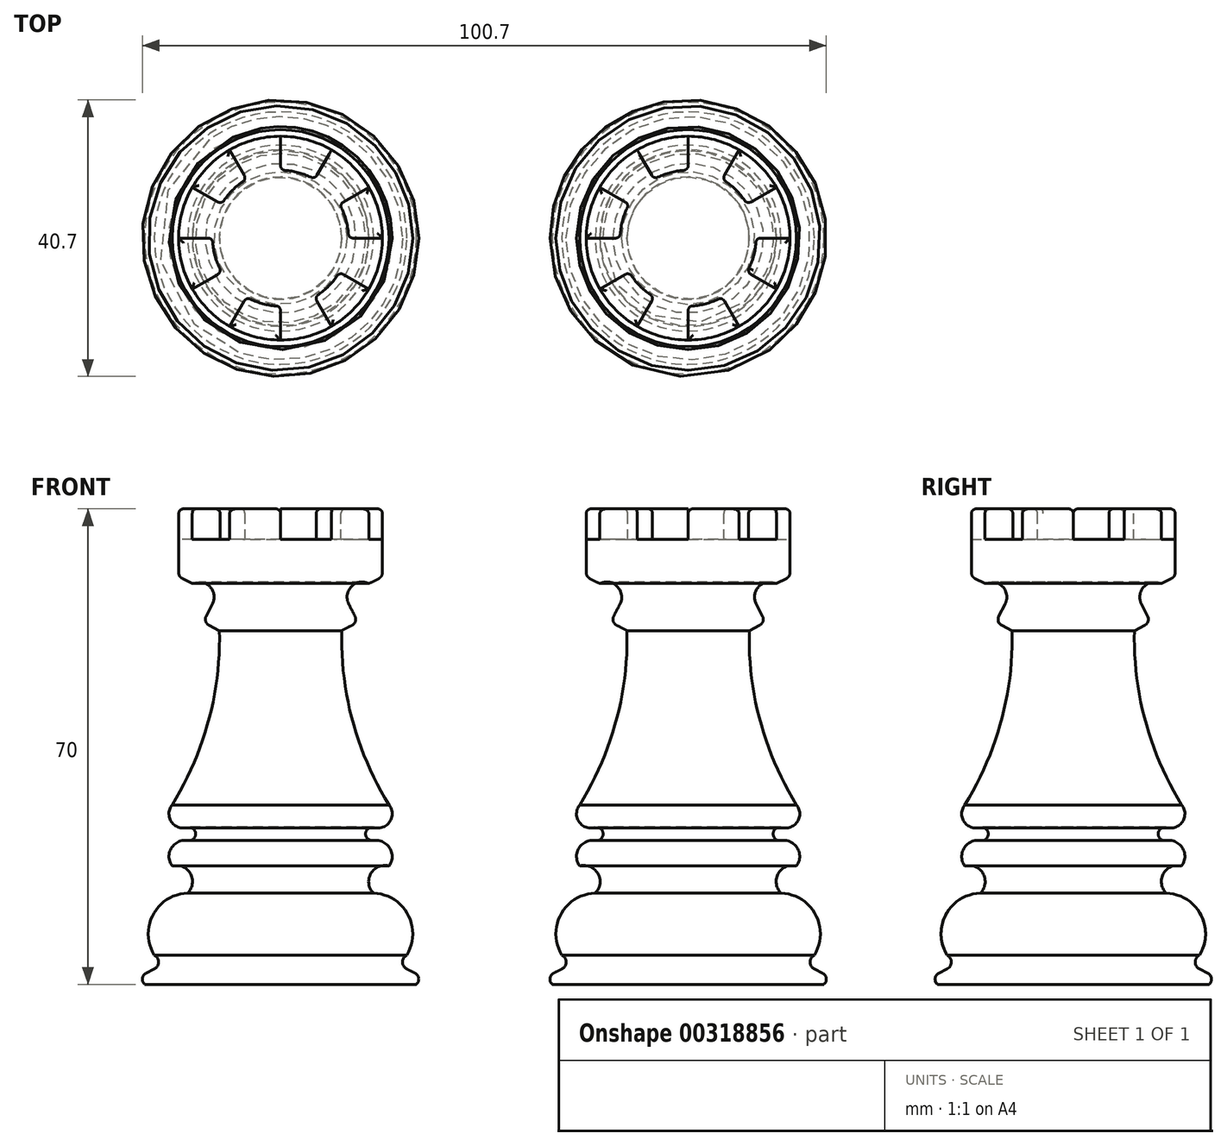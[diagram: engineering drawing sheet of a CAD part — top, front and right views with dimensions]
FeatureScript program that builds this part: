
annotation { "Feature Type Name" : "Feature", "Feature Type Description" : "" }
export const myFeature = defineFeature(function(context is Context, id is Id, definition is map)
    precondition{}
    {
        {
            var Q0;
            Q0=qCreatedBy(makeId("Front.planeOp"),FACE);
            var sketch = newSketch(context, id + "F0", { "sketchPlane" : qUnion([Q0])});
            skLineSegment(sketch, "E0", {"start": v(0, 35) * mm, "end": v(0, -35) * mm});
            skLineSegment(sketch, "E1", {"start": v(0, -35) * mm, "end": v(-20, -35) * mm});
            skLineSegment(sketch, "E2", {"start": v(0, 35) * mm, "end": v(-15, 35) * mm});
            skLineSegment(sketch, "E3", {"start": v(-15, 35) * mm, "end": v(-15, 25) * mm});
            skLineSegment(sketch, "E4", {"start": v(-20, -35) * mm, "end": v(-21.1, -34) * mm});
            skLineSegment(sketch, "E5", {"start": v(-21.1, -34) * mm, "end": v(-18.59, -32.74) * mm});
            skArc(sketch, "E6", {"start": v(-18.59, -32.74) * mm, "mid": v(-17.95, -31.72) * mm, "end": v(-18.59, -30.69) * mm});
            skArc(sketch, "E7", {"start": v(-13.69, -21.57) * mm, "mid": v(-18.76, -24.72) * mm, "end": v(-18.59, -30.69) * mm});
            skArc(sketch, "E8", {"start": v(-13.69, -21.57) * mm, "mid": v(-13.28, -18.7) * mm, "end": v(-15.97, -17.59) * mm});
            skArc(sketch, "E9", {"start": v(-13.69, -13.82) * mm, "mid": v(-16.08, -14.95) * mm, "end": v(-15.97, -17.59) * mm});
            skArc(sketch, "E10", {"start": v(-13.69, -13.82) * mm, "mid": v(-12.51, -12.86) * mm, "end": v(-13.69, -11.89) * mm});
            skArc(sketch, "E11", {"start": v(-15.97, -8.58) * mm, "mid": v(-16.06, -11.09) * mm, "end": v(-13.69, -11.89) * mm});
            skPoint(sketch, "E12.center.orphan", {"position": v(-14.66, 21) * mm});
            skPoint(sketch, "E12.end.orphan", {"position": v(-13, 24) * mm});
            skPoint(sketch, "E13.start.orphan", {"position": v(-9, 20.16) * mm});
            skPoint(sketch, "E14.end.orphan", {"position": v(-9, 17.08) * mm});
            skArc(sketch, "E15", {"start": v(-15.97, -8.58) * mm, "mid": v(-10.62, 3.74) * mm, "end": v(-9, 17.08) * mm});
            skLineSegment(sketch, "E16", {"start": v(-9, 17.08) * mm, "end": v(-11.4, 18.3) * mm});
            skLineSegment(sketch, "E17", {"start": v(-11.4, 18.3) * mm, "end": v(-10.03, 21) * mm});
            skArc(sketch, "E18", {"start": v(-10.03, 21) * mm, "mid": v(-10.43, 23.58) * mm, "end": v(-13, 24) * mm});
            skLineSegment(sketch, "E19", {"start": v(-15, 25) * mm, "end": v(-13, 24) * mm});
            skLineSegment(sketch, "E20", {"start": v(0, 44.63) * mm, "end": v(0, -39) * mm, "construction": true});
            skSolve(sketch);
        }
        {
            var Q0;
            Q0=makeQuery(id+"F0.imprint","IMPRINT",FACE,{"disambiguationData":[TD([[makeQuery(id+"F0.imprint","IMPRINT",EDGE,{"derivedFrom":sQuery(id+"F0.wireOp",EDGE,"E0")}),-1.0]])]});
            var Q1;
            Q1=sQuery(id+"F0.wireOp",EDGE,"E20");
            revolve(context, id + "F1", {"entities" : qUnion([Q0]), "axis" : qUnion([Q1]), "revolveType" : RevolveType.FULL});
        }
        {
            var Q0;
            Q0=makeQuery(id+"F1.opRevolve","SWEPT_EDGE",EDGE,{"disambiguationData":[OSD([sQuery(id+"F0.wireOp",EDGE,"E4"),sQuery(id+"F0.wireOp",EDGE,"E5")])]});
            var Q1;
            Q1=makeQuery(id+"F1.opRevolve","SWEPT_EDGE",EDGE,{"disambiguationData":[OSD([sQuery(id+"F0.wireOp",EDGE,"E16"),sQuery(id+"F0.wireOp",EDGE,"E17")])]});
            var Q2;
            Q2=makeQuery(id+"F1.opRevolve","SWEPT_EDGE",EDGE,{"disambiguationData":[OSD([sQuery(id+"F0.wireOp",EDGE,"E3"),sQuery(id+"F0.wireOp",EDGE,"E19")])]});
            fillet(context, id + "F2", {"entities" : qUnion([Q0, Q1, Q2]), "radius" : 1 * mm, "tangentPropagation" : true, "allowEdgeOverflow" : false});
        }
        {
            var Q0;
            Q0=qCreatedBy(makeId("Right.planeOp"),FACE);
            cPlane(context, id + "F3", {"entities" : qUnion([Q0]), "cplaneType" : CPlaneType.OFFSET, "offset" : 30 * mm, "width" : 150 * mm, "height" : 150 * mm});
        }
        {
            var Q0;
            Q0=makeQuery(id+"F1.opRevolve","SWEPT_FACE",FACE,{"disambiguationData":[OSD([sQuery(id+"F0.wireOp",EDGE,"E2")])]});
            var sketch = newSketch(context, id + "F4", { "sketchPlane" : qUnion([Q0])});
            skArc(sketch, "E21.0", {"start": v(5, 8.66) * mm, "mid": v(2.59, 9.66) * mm, "end": v(0, 10) * mm});
            skArc(sketch, "E22.cCircle", {"start": v(5, 8.66) * mm, "mid": v(2.59, 9.66) * mm, "end": v(0, 10) * mm, "construction": true});
            skLineSegment(sketch, "E22.0", {"start": v(0, 10) * mm, "end": v(5, 8.66) * mm, "construction": true});
            skLineSegment(sketch, "E22.2", {"start": v(8.66, 5) * mm, "end": v(10, 0) * mm, "construction": true});
            skLineSegment(sketch, "E22.4", {"start": v(8.66, -5) * mm, "end": v(5, -8.66) * mm, "construction": true});
            skLineSegment(sketch, "E22.6", {"start": v(0, -10) * mm, "end": v(-5, -8.66) * mm, "construction": true});
            skLineSegment(sketch, "E22.8", {"start": v(-8.66, -5) * mm, "end": v(-10, 0) * mm, "construction": true});
            skLineSegment(sketch, "E22.10", {"start": v(-8.66, 5) * mm, "end": v(-5, 8.66) * mm, "construction": true});
            skCircle(sketch, "E23.cCircle", {"center": v(0, 0) * mm, "radius": 15 * mm, "construction": true});
            skLineSegment(sketch, "E23.0", {"start": v(0, 15) * mm, "end": v(7.5, 13) * mm, "construction": true});
            skLineSegment(sketch, "E23.1", {"start": v(7.5, 13) * mm, "end": v(13, 7.5) * mm, "construction": true});
            skLineSegment(sketch, "E23.2", {"start": v(13, 7.5) * mm, "end": v(15, 0) * mm, "construction": true});
            skLineSegment(sketch, "E23.3", {"start": v(15, 0) * mm, "end": v(13, -7.5) * mm, "construction": true});
            skLineSegment(sketch, "E23.4", {"start": v(13, -7.5) * mm, "end": v(7.5, -13) * mm, "construction": true});
            skLineSegment(sketch, "E23.5", {"start": v(7.5, -13) * mm, "end": v(0, -15) * mm, "construction": true});
            skLineSegment(sketch, "E23.6", {"start": v(0, -15) * mm, "end": v(-7.5, -13) * mm, "construction": true});
            skLineSegment(sketch, "E23.7", {"start": v(-7.5, -13) * mm, "end": v(-13, -7.5) * mm, "construction": true});
            skLineSegment(sketch, "E23.8", {"start": v(-13, -7.5) * mm, "end": v(-15, 0) * mm, "construction": true});
            skLineSegment(sketch, "E23.9", {"start": v(-15, 0) * mm, "end": v(-13, 7.5) * mm, "construction": true});
            skLineSegment(sketch, "E23.10", {"start": v(-13, 7.5) * mm, "end": v(-7.5, 13) * mm, "construction": true});
            skLineSegment(sketch, "E23.11", {"start": v(-7.5, 13) * mm, "end": v(0, 15) * mm, "construction": true});
            skLineSegment(sketch, "E24", {"start": v(0, 10) * mm, "end": v(0, 15) * mm});
            skLineSegment(sketch, "E25", {"start": v(5, 8.66) * mm, "end": v(7.5, 13) * mm});
            skLineSegment(sketch, "E26", {"start": v(8.66, 5) * mm, "end": v(13, 7.5) * mm});
            skLineSegment(sketch, "E27", {"start": v(10, 0) * mm, "end": v(15, 0) * mm});
            skLineSegment(sketch, "E28", {"start": v(8.66, -5) * mm, "end": v(13, -7.5) * mm});
            skLineSegment(sketch, "E29", {"start": v(5, -8.66) * mm, "end": v(7.5, -13) * mm});
            skLineSegment(sketch, "E30", {"start": v(0, -10) * mm, "end": v(0, -15) * mm});
            skLineSegment(sketch, "E31", {"start": v(-5, -8.66) * mm, "end": v(-7.5, -13) * mm});
            skLineSegment(sketch, "E32", {"start": v(-8.66, -5) * mm, "end": v(-13, -7.5) * mm});
            skLineSegment(sketch, "E33", {"start": v(-10, 0) * mm, "end": v(-15, 0) * mm});
            skLineSegment(sketch, "E34", {"start": v(-8.66, 5) * mm, "end": v(-13, 7.5) * mm});
            skLineSegment(sketch, "E35", {"start": v(-5, 8.66) * mm, "end": v(-7.5, 13) * mm});
            skArc(sketch, "E36.trimOffspring", {"start": v(10, 0) * mm, "mid": v(9.66, 2.59) * mm, "end": v(8.66, 5) * mm, "construction": true});
            skArc(sketch, "E37.trimOffspring", {"start": v(10, 0) * mm, "mid": v(9.66, 2.59) * mm, "end": v(8.66, 5) * mm});
            skArc(sketch, "E38.trimOffspring", {"start": v(5, -8.66) * mm, "mid": v(7.07, -7.07) * mm, "end": v(8.66, -5) * mm, "construction": true});
            skArc(sketch, "E39.trimOffspring", {"start": v(5, -8.66) * mm, "mid": v(7.07, -7.07) * mm, "end": v(8.66, -5) * mm});
            skArc(sketch, "E40.trimOffspring", {"start": v(-5, -8.66) * mm, "mid": v(-2.59, -9.66) * mm, "end": v(0, -10) * mm, "construction": true});
            skArc(sketch, "E41.trimOffspring", {"start": v(-5, -8.66) * mm, "mid": v(-2.59, -9.66) * mm, "end": v(0, -10) * mm});
            skArc(sketch, "E42.trimOffspring", {"start": v(-10, 0) * mm, "mid": v(-9.66, -2.59) * mm, "end": v(-8.66, -5) * mm, "construction": true});
            skArc(sketch, "E43.trimOffspring", {"start": v(-10, 0) * mm, "mid": v(-9.66, -2.59) * mm, "end": v(-8.66, -5) * mm});
            skArc(sketch, "E44.trimOffspring", {"start": v(-5, 8.66) * mm, "mid": v(-7.07, 7.07) * mm, "end": v(-8.66, 5) * mm, "construction": true});
            skArc(sketch, "E45.trimOffspring", {"start": v(-5, 8.66) * mm, "mid": v(-7.07, 7.07) * mm, "end": v(-8.66, 5) * mm});
            skSolve(sketch);
        }
        {
            var Q0;
            Q0=makeQuery(id+"F4.imprint","IMPRINT",FACE,{"disambiguationData":[TD([[makeQuery(id+"F4.imprint","IMPRINT",EDGE,{"derivedFrom":sQuery(id+"F4.wireOp",EDGE,"E21.0")}),1.0]])]});
            extrude(context, id + "F5", {"entities" : qUnion([Q0]), "operationType" : NewBodyOperationType.REMOVE, "oppositeDirection" : true, "depth" : 4.5 * mm});
        }
        {
            var Q0;
            {var subQ0=sQuery(id+"F0.wireOp",EDGE,"E3");var subQ1=sQuery(id+"F0.wireOp",EDGE,"E2");var subQ2=makeQuery(id+"F1.opRevolve","SWEPT_EDGE",EDGE,{"disambiguationData":[OSD([subQ1,subQ0])]});Q0=makeQuery(id+"F5.boolean.opBoolean","COPY",EDGE,{"derivedFrom":makeQuery(id+"F5.opExtrude","CAP_EDGE",EDGE,{"disambiguationData":[OSD([subQ1,subQ0]),TDD([makeQuery(id+"F4.imprint","IMPRINT",EDGE,{"disambiguationData":[TD([[makeQuery(id+"F4.imprint","INTERSECT",VERTEX,{"derivedFrom":[subQ2,sQuery(id+"F4.wireOp",EDGE,"E27")]}),1.0]])],"derivedFrom":subQ2})])],"isStart":false})});}
            var Q1;
            Q1=makeQuery(id+"F5.boolean.opBoolean","COPY",EDGE,{"derivedFrom":makeQuery(id+"F5.opExtrude","SWEPT_EDGE",EDGE,{"disambiguationData":[OSD([sQuery(id+"F0.wireOp",EDGE,"E2"),sQuery(id+"F0.wireOp",EDGE,"E3"),sQuery(id+"F4.wireOp",EDGE,"E28")])]})});
            var Q2;
            {var subQ0=sQuery(id+"F0.wireOp",EDGE,"E3");var subQ1=sQuery(id+"F0.wireOp",EDGE,"E2");var subQ2=makeQuery(id+"F1.opRevolve","SWEPT_EDGE",EDGE,{"disambiguationData":[OSD([subQ1,subQ0])]});Q2=makeQuery(id+"F5.boolean.opBoolean","COPY",EDGE,{"derivedFrom":makeQuery(id+"F5.opExtrude","CAP_EDGE",EDGE,{"disambiguationData":[OSD([subQ1,subQ0]),TDD([makeQuery(id+"F4.imprint","IMPRINT",EDGE,{"disambiguationData":[TD([[makeQuery(id+"F4.imprint","INTERSECT",VERTEX,{"derivedFrom":[subQ2,sQuery(id+"F4.wireOp",EDGE,"E29")]}),1.0]])],"derivedFrom":subQ2})])],"isStart":false})});}
            var Q3;
            Q3=makeQuery(id+"F5.boolean.opBoolean","COPY",EDGE,{"derivedFrom":makeQuery(id+"F5.opExtrude","SWEPT_EDGE",EDGE,{"disambiguationData":[OSD([sQuery(id+"F0.wireOp",EDGE,"E2"),sQuery(id+"F0.wireOp",EDGE,"E3"),sQuery(id+"F4.wireOp",EDGE,"E29")])]})});
            var Q4;
            {var subQ0=sQuery(id+"F0.wireOp",EDGE,"E2");var subQ1=sQuery(id+"F0.wireOp",EDGE,"E3");Q4=makeQuery(id+"F5.boolean.opBoolean","SPLIT",EDGE,{"disambiguationData":[TD([makeQuery(id+"F5.opExtrude","SWEPT_FACE",FACE,{"disambiguationData":[OSD([sQuery(id+"F4.wireOp",EDGE,"E28")])]})])],"derivedFrom":makeQuery(id+"F1.opRevolve","SWEPT_EDGE",EDGE,{"disambiguationData":[OSD([subQ0,subQ1])]})});}
            var Q5;
            Q5=makeQuery(id+"F5.boolean.opBoolean","COPY",EDGE,{"derivedFrom":makeQuery(id+"F5.opExtrude","SWEPT_EDGE",EDGE,{"disambiguationData":[OSD([sQuery(id+"F0.wireOp",EDGE,"E2"),sQuery(id+"F0.wireOp",EDGE,"E3"),sQuery(id+"F4.wireOp",EDGE,"E30")])]})});
            var Q6;
            {var subQ0=sQuery(id+"F0.wireOp",EDGE,"E2");var subQ1=sQuery(id+"F0.wireOp",EDGE,"E3");Q6=makeQuery(id+"F5.boolean.opBoolean","SPLIT",EDGE,{"disambiguationData":[TD([makeQuery(id+"F5.opExtrude","SWEPT_FACE",FACE,{"disambiguationData":[OSD([sQuery(id+"F4.wireOp",EDGE,"E30")])]})])],"derivedFrom":makeQuery(id+"F1.opRevolve","SWEPT_EDGE",EDGE,{"disambiguationData":[OSD([subQ0,subQ1])]})});}
            var Q7;
            Q7=makeQuery(id+"F5.boolean.opBoolean","COPY",EDGE,{"derivedFrom":makeQuery(id+"F5.opExtrude","SWEPT_EDGE",EDGE,{"disambiguationData":[OSD([sQuery(id+"F0.wireOp",EDGE,"E2"),sQuery(id+"F0.wireOp",EDGE,"E3"),sQuery(id+"F4.wireOp",EDGE,"E31")])]})});
            var Q8;
            {var subQ0=sQuery(id+"F0.wireOp",EDGE,"E3");var subQ1=sQuery(id+"F0.wireOp",EDGE,"E2");var subQ2=makeQuery(id+"F1.opRevolve","SWEPT_EDGE",EDGE,{"disambiguationData":[OSD([subQ1,subQ0])]});Q8=makeQuery(id+"F5.boolean.opBoolean","COPY",EDGE,{"derivedFrom":makeQuery(id+"F5.opExtrude","CAP_EDGE",EDGE,{"disambiguationData":[OSD([subQ1,subQ0]),TDD([makeQuery(id+"F4.imprint","IMPRINT",EDGE,{"disambiguationData":[TD([[makeQuery(id+"F4.imprint","INTERSECT",VERTEX,{"derivedFrom":[subQ2,sQuery(id+"F4.wireOp",EDGE,"E31")]}),1.0]])],"derivedFrom":subQ2})])],"isStart":false})});}
            var Q9;
            Q9=makeQuery(id+"F5.boolean.opBoolean","COPY",EDGE,{"derivedFrom":makeQuery(id+"F5.opExtrude","SWEPT_EDGE",EDGE,{"disambiguationData":[OSD([sQuery(id+"F0.wireOp",EDGE,"E2"),sQuery(id+"F0.wireOp",EDGE,"E3"),sQuery(id+"F4.wireOp",EDGE,"E32")])]})});
            var Q10;
            {var subQ0=sQuery(id+"F0.wireOp",EDGE,"E2");var subQ1=sQuery(id+"F0.wireOp",EDGE,"E3");Q10=makeQuery(id+"F5.boolean.opBoolean","SPLIT",EDGE,{"disambiguationData":[TD([makeQuery(id+"F5.opExtrude","SWEPT_FACE",FACE,{"disambiguationData":[OSD([sQuery(id+"F4.wireOp",EDGE,"E32")])]})])],"derivedFrom":makeQuery(id+"F1.opRevolve","SWEPT_EDGE",EDGE,{"disambiguationData":[OSD([subQ0,subQ1])]})});}
            var Q11;
            {var subQ0=sQuery(id+"F0.wireOp",EDGE,"E3");var subQ1=sQuery(id+"F0.wireOp",EDGE,"E2");var subQ2=makeQuery(id+"F1.opRevolve","SWEPT_EDGE",EDGE,{"disambiguationData":[OSD([subQ1,subQ0])]});Q11=makeQuery(id+"F5.boolean.opBoolean","COPY",EDGE,{"derivedFrom":makeQuery(id+"F5.opExtrude","CAP_EDGE",EDGE,{"disambiguationData":[OSD([subQ1,subQ0]),TDD([makeQuery(id+"F4.imprint","IMPRINT",EDGE,{"disambiguationData":[TD([[makeQuery(id+"F4.imprint","INTERSECT",VERTEX,{"derivedFrom":[subQ2,sQuery(id+"F4.wireOp",EDGE,"E33")]}),1.0]])],"derivedFrom":subQ2})])],"isStart":false})});}
            var Q12;
            {var subQ0=sQuery(id+"F0.wireOp",EDGE,"E3");var subQ1=sQuery(id+"F0.wireOp",EDGE,"E2");var subQ2=makeQuery(id+"F1.opRevolve","SWEPT_EDGE",EDGE,{"disambiguationData":[OSD([subQ1,subQ0])]});Q12=makeQuery(id+"F5.boolean.opBoolean","COPY",EDGE,{"derivedFrom":makeQuery(id+"F5.opExtrude","CAP_EDGE",EDGE,{"disambiguationData":[OSD([subQ1,subQ0]),TDD([makeQuery(id+"F4.imprint","IMPRINT",EDGE,{"disambiguationData":[TD([[makeQuery(id+"F4.imprint","INTERSECT",VERTEX,{"derivedFrom":[subQ2,sQuery(id+"F4.wireOp",EDGE,"E24")]}),-1.0]])],"derivedFrom":subQ2})])],"isStart":false})});}
            var Q13;
            {var subQ0=sQuery(id+"F0.wireOp",EDGE,"E3");var subQ1=sQuery(id+"F0.wireOp",EDGE,"E2");var subQ2=makeQuery(id+"F1.opRevolve","SWEPT_EDGE",EDGE,{"disambiguationData":[OSD([subQ1,subQ0])]});Q13=makeQuery(id+"F5.boolean.opBoolean","COPY",EDGE,{"derivedFrom":makeQuery(id+"F5.opExtrude","CAP_EDGE",EDGE,{"disambiguationData":[OSD([subQ1,subQ0]),TDD([makeQuery(id+"F4.imprint","IMPRINT",EDGE,{"disambiguationData":[TD([[makeQuery(id+"F4.imprint","INTERSECT",VERTEX,{"derivedFrom":[subQ2,sQuery(id+"F4.wireOp",EDGE,"E25")]}),1.0]])],"derivedFrom":subQ2})])],"isStart":false})});}
            var Q14;
            {var subQ0=sQuery(id+"F0.wireOp",EDGE,"E2");var subQ1=sQuery(id+"F0.wireOp",EDGE,"E3");Q14=makeQuery(id+"F5.boolean.opBoolean","SPLIT",EDGE,{"disambiguationData":[TD([makeQuery(id+"F5.opExtrude","SWEPT_FACE",FACE,{"disambiguationData":[OSD([sQuery(id+"F4.wireOp",EDGE,"E34")])]})])],"derivedFrom":makeQuery(id+"F1.opRevolve","SWEPT_EDGE",EDGE,{"disambiguationData":[OSD([subQ0,subQ1])]})});}
            var Q15;
            {var subQ0=sQuery(id+"F0.wireOp",EDGE,"E2");var subQ1=sQuery(id+"F0.wireOp",EDGE,"E3");Q15=makeQuery(id+"F5.boolean.opBoolean","SPLIT",EDGE,{"disambiguationData":[TD([makeQuery(id+"F5.opExtrude","SWEPT_FACE",FACE,{"disambiguationData":[OSD([sQuery(id+"F4.wireOp",EDGE,"E24")])]})])],"derivedFrom":makeQuery(id+"F1.opRevolve","SWEPT_EDGE",EDGE,{"disambiguationData":[OSD([subQ0,subQ1])]})});}
            var Q16;
            {var subQ0=sQuery(id+"F0.wireOp",EDGE,"E2");var subQ1=sQuery(id+"F0.wireOp",EDGE,"E3");Q16=makeQuery(id+"F5.boolean.opBoolean","SPLIT",EDGE,{"disambiguationData":[TD([makeQuery(id+"F5.opExtrude","SWEPT_FACE",FACE,{"disambiguationData":[OSD([sQuery(id+"F4.wireOp",EDGE,"E26")])]})])],"derivedFrom":makeQuery(id+"F1.opRevolve","SWEPT_EDGE",EDGE,{"disambiguationData":[OSD([subQ0,subQ1])]})});}
            var Q17;
            Q17=makeQuery(id+"F5.boolean.opBoolean","COPY",EDGE,{"derivedFrom":makeQuery(id+"F5.opExtrude","CAP_EDGE",EDGE,{"disambiguationData":[OSD([sQuery(id+"F4.wireOp",EDGE,"E24")])],"isStart":true})});
            var Q18;
            Q18=makeQuery(id+"F5.boolean.opBoolean","COPY",EDGE,{"derivedFrom":makeQuery(id+"F5.opExtrude","CAP_EDGE",EDGE,{"disambiguationData":[OSD([sQuery(id+"F4.wireOp",EDGE,"E21.0")])],"isStart":true})});
            var Q19;
            Q19=makeQuery(id+"F5.boolean.opBoolean","COPY",EDGE,{"derivedFrom":makeQuery(id+"F5.opExtrude","CAP_EDGE",EDGE,{"disambiguationData":[OSD([sQuery(id+"F4.wireOp",EDGE,"E25")])],"isStart":true})});
            var Q20;
            Q20=makeQuery(id+"F5.boolean.opBoolean","COPY",EDGE,{"derivedFrom":makeQuery(id+"F5.opExtrude","CAP_EDGE",EDGE,{"disambiguationData":[OSD([sQuery(id+"F4.wireOp",EDGE,"E26")])],"isStart":true})});
            var Q21;
            Q21=makeQuery(id+"F5.boolean.opBoolean","COPY",EDGE,{"derivedFrom":makeQuery(id+"F5.opExtrude","CAP_EDGE",EDGE,{"disambiguationData":[OSD([sQuery(id+"F4.wireOp",EDGE,"E37.trimOffspring")])],"isStart":true})});
            var Q22;
            Q22=makeQuery(id+"F5.boolean.opBoolean","COPY",EDGE,{"derivedFrom":makeQuery(id+"F5.opExtrude","CAP_EDGE",EDGE,{"disambiguationData":[OSD([sQuery(id+"F4.wireOp",EDGE,"E27")])],"isStart":true})});
            var Q23;
            Q23=makeQuery(id+"F5.boolean.opBoolean","COPY",EDGE,{"derivedFrom":makeQuery(id+"F5.opExtrude","CAP_EDGE",EDGE,{"disambiguationData":[OSD([sQuery(id+"F4.wireOp",EDGE,"E28")])],"isStart":true})});
            var Q24;
            Q24=makeQuery(id+"F5.boolean.opBoolean","COPY",EDGE,{"derivedFrom":makeQuery(id+"F5.opExtrude","CAP_EDGE",EDGE,{"disambiguationData":[OSD([sQuery(id+"F4.wireOp",EDGE,"E39.trimOffspring")])],"isStart":true})});
            var Q25;
            Q25=makeQuery(id+"F5.boolean.opBoolean","COPY",EDGE,{"derivedFrom":makeQuery(id+"F5.opExtrude","CAP_EDGE",EDGE,{"disambiguationData":[OSD([sQuery(id+"F4.wireOp",EDGE,"E29")])],"isStart":true})});
            var Q26;
            Q26=makeQuery(id+"F5.boolean.opBoolean","COPY",EDGE,{"derivedFrom":makeQuery(id+"F5.opExtrude","CAP_EDGE",EDGE,{"disambiguationData":[OSD([sQuery(id+"F4.wireOp",EDGE,"E30")])],"isStart":true})});
            var Q27;
            Q27=makeQuery(id+"F5.boolean.opBoolean","COPY",EDGE,{"derivedFrom":makeQuery(id+"F5.opExtrude","CAP_EDGE",EDGE,{"disambiguationData":[OSD([sQuery(id+"F4.wireOp",EDGE,"E41.trimOffspring")])],"isStart":true})});
            var Q28;
            Q28=makeQuery(id+"F5.boolean.opBoolean","COPY",EDGE,{"derivedFrom":makeQuery(id+"F5.opExtrude","CAP_EDGE",EDGE,{"disambiguationData":[OSD([sQuery(id+"F4.wireOp",EDGE,"E31")])],"isStart":true})});
            var Q29;
            Q29=makeQuery(id+"F5.boolean.opBoolean","COPY",EDGE,{"derivedFrom":makeQuery(id+"F5.opExtrude","CAP_EDGE",EDGE,{"disambiguationData":[OSD([sQuery(id+"F4.wireOp",EDGE,"E32")])],"isStart":true})});
            var Q30;
            Q30=makeQuery(id+"F5.boolean.opBoolean","COPY",EDGE,{"derivedFrom":makeQuery(id+"F5.opExtrude","CAP_EDGE",EDGE,{"disambiguationData":[OSD([sQuery(id+"F4.wireOp",EDGE,"E43.trimOffspring")])],"isStart":true})});
            var Q31;
            Q31=makeQuery(id+"F5.boolean.opBoolean","COPY",EDGE,{"derivedFrom":makeQuery(id+"F5.opExtrude","CAP_EDGE",EDGE,{"disambiguationData":[OSD([sQuery(id+"F4.wireOp",EDGE,"E33")])],"isStart":true})});
            var Q32;
            Q32=makeQuery(id+"F5.boolean.opBoolean","COPY",EDGE,{"derivedFrom":makeQuery(id+"F5.opExtrude","CAP_EDGE",EDGE,{"disambiguationData":[OSD([sQuery(id+"F4.wireOp",EDGE,"E34")])],"isStart":true})});
            var Q33;
            Q33=makeQuery(id+"F5.boolean.opBoolean","COPY",EDGE,{"derivedFrom":makeQuery(id+"F5.opExtrude","CAP_EDGE",EDGE,{"disambiguationData":[OSD([sQuery(id+"F4.wireOp",EDGE,"E45.trimOffspring")])],"isStart":true})});
            var Q34;
            Q34=makeQuery(id+"F5.boolean.opBoolean","COPY",EDGE,{"derivedFrom":makeQuery(id+"F5.opExtrude","CAP_EDGE",EDGE,{"disambiguationData":[OSD([sQuery(id+"F4.wireOp",EDGE,"E35")])],"isStart":true})});
            var Q35;
            Q35=makeQuery(id+"F5.boolean.opBoolean","COPY",EDGE,{"derivedFrom":makeQuery(id+"F5.opExtrude","SWEPT_EDGE",EDGE,{"disambiguationData":[OSD([sQuery(id+"F0.wireOp",EDGE,"E2"),sQuery(id+"F0.wireOp",EDGE,"E3"),sQuery(id+"F4.wireOp",EDGE,"E33")])]})});
            var Q36;
            Q36=makeQuery(id+"F5.boolean.opBoolean","COPY",EDGE,{"derivedFrom":makeQuery(id+"F5.opExtrude","SWEPT_EDGE",EDGE,{"disambiguationData":[OSD([sQuery(id+"F0.wireOp",EDGE,"E2"),sQuery(id+"F0.wireOp",EDGE,"E3"),sQuery(id+"F4.wireOp",EDGE,"E34")])]})});
            var Q37;
            Q37=makeQuery(id+"F5.boolean.opBoolean","COPY",EDGE,{"derivedFrom":makeQuery(id+"F5.opExtrude","SWEPT_EDGE",EDGE,{"disambiguationData":[OSD([sQuery(id+"F0.wireOp",EDGE,"E2"),sQuery(id+"F0.wireOp",EDGE,"E3"),sQuery(id+"F4.wireOp",EDGE,"E35")])]})});
            var Q38;
            Q38=makeQuery(id+"F5.boolean.opBoolean","COPY",EDGE,{"derivedFrom":makeQuery(id+"F5.opExtrude","SWEPT_EDGE",EDGE,{"disambiguationData":[OSD([sQuery(id+"F0.wireOp",EDGE,"E2"),sQuery(id+"F0.wireOp",EDGE,"E3"),sQuery(id+"F4.wireOp",EDGE,"E24")])]})});
            var Q39;
            Q39=makeQuery(id+"F5.boolean.opBoolean","COPY",EDGE,{"derivedFrom":makeQuery(id+"F5.opExtrude","SWEPT_EDGE",EDGE,{"disambiguationData":[OSD([sQuery(id+"F0.wireOp",EDGE,"E2"),sQuery(id+"F0.wireOp",EDGE,"E3"),sQuery(id+"F4.wireOp",EDGE,"E25")])]})});
            var Q40;
            Q40=makeQuery(id+"F5.boolean.opBoolean","COPY",EDGE,{"derivedFrom":makeQuery(id+"F5.opExtrude","SWEPT_EDGE",EDGE,{"disambiguationData":[OSD([sQuery(id+"F0.wireOp",EDGE,"E2"),sQuery(id+"F0.wireOp",EDGE,"E3"),sQuery(id+"F4.wireOp",EDGE,"E26")])]})});
            var Q41;
            Q41=makeQuery(id+"F5.boolean.opBoolean","COPY",EDGE,{"derivedFrom":makeQuery(id+"F5.opExtrude","SWEPT_EDGE",EDGE,{"disambiguationData":[OSD([sQuery(id+"F0.wireOp",EDGE,"E2"),sQuery(id+"F0.wireOp",EDGE,"E3"),sQuery(id+"F4.wireOp",EDGE,"E27")])]})});
            var Q42;
            Q42=makeQuery(id+"F5.boolean.opBoolean","COPY",EDGE,{"derivedFrom":makeQuery(id+"F5.opExtrude","SWEPT_EDGE",EDGE,{"disambiguationData":[OSD([sQuery(id+"F4.wireOp",EDGE,"E32"),sQuery(id+"F4.wireOp",EDGE,"E43.trimOffspring")])]})});
            var Q43;
            Q43=makeQuery(id+"F5.boolean.opBoolean","COPY",EDGE,{"derivedFrom":makeQuery(id+"F5.opExtrude","SWEPT_EDGE",EDGE,{"disambiguationData":[OSD([sQuery(id+"F4.wireOp",EDGE,"E33"),sQuery(id+"F4.wireOp",EDGE,"E43.trimOffspring")])]})});
            var Q44;
            Q44=makeQuery(id+"F5.boolean.opBoolean","COPY",EDGE,{"derivedFrom":makeQuery(id+"F5.opExtrude","SWEPT_EDGE",EDGE,{"disambiguationData":[OSD([sQuery(id+"F4.wireOp",EDGE,"E34"),sQuery(id+"F4.wireOp",EDGE,"E45.trimOffspring")])]})});
            var Q45;
            Q45=makeQuery(id+"F5.boolean.opBoolean","COPY",EDGE,{"derivedFrom":makeQuery(id+"F5.opExtrude","SWEPT_EDGE",EDGE,{"disambiguationData":[OSD([sQuery(id+"F4.wireOp",EDGE,"E35"),sQuery(id+"F4.wireOp",EDGE,"E45.trimOffspring")])]})});
            var Q46;
            Q46=makeQuery(id+"F5.boolean.opBoolean","COPY",EDGE,{"derivedFrom":makeQuery(id+"F5.opExtrude","SWEPT_EDGE",EDGE,{"disambiguationData":[OSD([sQuery(id+"F4.wireOp",EDGE,"E21.0"),sQuery(id+"F4.wireOp",EDGE,"E24")])]})});
            var Q47;
            Q47=makeQuery(id+"F5.boolean.opBoolean","COPY",EDGE,{"derivedFrom":makeQuery(id+"F5.opExtrude","SWEPT_EDGE",EDGE,{"disambiguationData":[OSD([sQuery(id+"F4.wireOp",EDGE,"E21.0"),sQuery(id+"F4.wireOp",EDGE,"E25")])]})});
            var Q48;
            Q48=makeQuery(id+"F5.boolean.opBoolean","COPY",EDGE,{"derivedFrom":makeQuery(id+"F5.opExtrude","SWEPT_EDGE",EDGE,{"disambiguationData":[OSD([sQuery(id+"F4.wireOp",EDGE,"E26"),sQuery(id+"F4.wireOp",EDGE,"E37.trimOffspring")])]})});
            var Q49;
            Q49=makeQuery(id+"F5.boolean.opBoolean","COPY",EDGE,{"derivedFrom":makeQuery(id+"F5.opExtrude","SWEPT_EDGE",EDGE,{"disambiguationData":[OSD([sQuery(id+"F4.wireOp",EDGE,"E27"),sQuery(id+"F4.wireOp",EDGE,"E37.trimOffspring")])]})});
            var Q50;
            Q50=makeQuery(id+"F5.boolean.opBoolean","COPY",EDGE,{"derivedFrom":makeQuery(id+"F5.opExtrude","SWEPT_EDGE",EDGE,{"disambiguationData":[OSD([sQuery(id+"F4.wireOp",EDGE,"E28"),sQuery(id+"F4.wireOp",EDGE,"E39.trimOffspring")])]})});
            var Q51;
            Q51=makeQuery(id+"F5.boolean.opBoolean","COPY",EDGE,{"derivedFrom":makeQuery(id+"F5.opExtrude","SWEPT_EDGE",EDGE,{"disambiguationData":[OSD([sQuery(id+"F4.wireOp",EDGE,"E29"),sQuery(id+"F4.wireOp",EDGE,"E39.trimOffspring")])]})});
            var Q52;
            Q52=makeQuery(id+"F5.boolean.opBoolean","COPY",EDGE,{"derivedFrom":makeQuery(id+"F5.opExtrude","SWEPT_EDGE",EDGE,{"disambiguationData":[OSD([sQuery(id+"F4.wireOp",EDGE,"E30"),sQuery(id+"F4.wireOp",EDGE,"E41.trimOffspring")])]})});
            var Q53;
            Q53=makeQuery(id+"F5.boolean.opBoolean","COPY",EDGE,{"derivedFrom":makeQuery(id+"F5.opExtrude","SWEPT_EDGE",EDGE,{"disambiguationData":[OSD([sQuery(id+"F4.wireOp",EDGE,"E31"),sQuery(id+"F4.wireOp",EDGE,"E41.trimOffspring")])]})});
            fillet(context, id + "F6", {"entities" : qUnion([Q0, Q1, Q2, Q3, Q4, Q5, Q6, Q7, Q8, Q9, Q10, Q11, Q12, Q13, Q14, Q15, Q16, Q17, Q18, Q19, Q20, Q21, Q22, Q23, Q24, Q25, Q26, Q27, Q28, Q29, Q30, Q31, Q32, Q33, Q34, Q35, Q36, Q37, Q38, Q39, Q40, Q41, Q42, Q43, Q44, Q45, Q46, Q47, Q48, Q49, Q50, Q51, Q52, Q53]), "radius" : 0.7 * mm, "tangentPropagation" : true, "allowEdgeOverflow" : false});
        }
        {
            var Q0;
            Q0=makeQuery(id+"F1.opRevolve","SWEPT_BODY",BODY,{"disambiguationData":[OSD([sQuery(id+"F0.wireOp",EDGE,"E0"),sQuery(id+"F0.wireOp",EDGE,"E1"),sQuery(id+"F0.wireOp",EDGE,"E2"),sQuery(id+"F0.wireOp",EDGE,"E3"),sQuery(id+"F0.wireOp",EDGE,"E4"),sQuery(id+"F0.wireOp",EDGE,"E5"),sQuery(id+"F0.wireOp",EDGE,"E6"),sQuery(id+"F0.wireOp",EDGE,"E7"),sQuery(id+"F0.wireOp",EDGE,"E8"),sQuery(id+"F0.wireOp",EDGE,"E9"),sQuery(id+"F0.wireOp",EDGE,"E10"),sQuery(id+"F0.wireOp",EDGE,"E11"),sQuery(id+"F0.wireOp",EDGE,"E15"),sQuery(id+"F0.wireOp",EDGE,"E16"),sQuery(id+"F0.wireOp",EDGE,"E17"),sQuery(id+"F0.wireOp",EDGE,"E18"),sQuery(id+"F0.wireOp",EDGE,"E19")])]});
            var Q1;
            Q1=qCreatedBy(id+"F3.planeOp",FACE);
            mirror(context, id + "F7", {"entities" : qUnion([Q0]), "mirrorPlane" : qUnion([Q1])});
        }
    });
